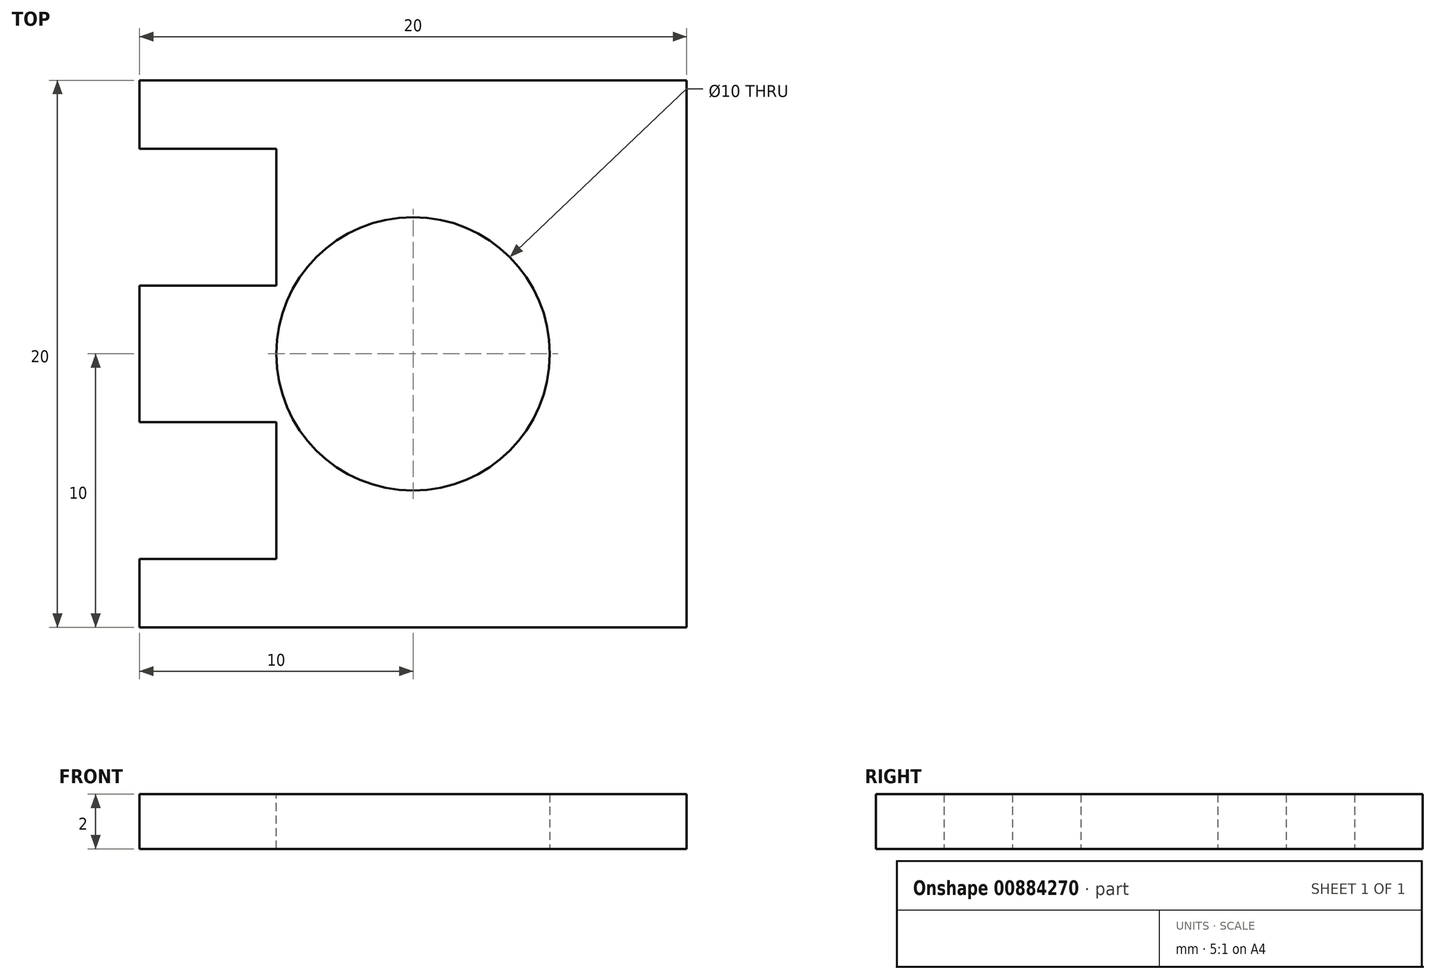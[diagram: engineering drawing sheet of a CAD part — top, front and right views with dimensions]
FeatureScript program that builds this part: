
annotation { "Feature Type Name" : "Feature", "Feature Type Description" : "" }
export const myFeature = defineFeature(function(context is Context, id is Id, definition is map)
    precondition{}
    {
        {
            var Q0;
            Q0=qCreatedBy(makeId("Top.planeOp"),FACE);
            var sketch = newSketch(context, id + "F0", { "sketchPlane" : qUnion([Q0])});
            skLineSegment(sketch, "E0.bottom", {"start": v(10, -10) * mm, "end": v(-10, -10) * mm});
            skLineSegment(sketch, "E0.top", {"start": v(10, 10) * mm, "end": v(-10, 10) * mm});
            skLineSegment(sketch, "E0.left", {"start": v(10, -10) * mm, "end": v(10, 10) * mm});
            skLineSegment(sketch, "E0.right", {"start": v(-10, -10) * mm, "end": v(-10, 10) * mm});
            skPoint(sketch, "E0.middle", {"position": v(0, 0) * mm});
            skCircle(sketch, "E1", {"center": v(0, 0) * mm, "radius": 5 * mm});
            skSolve(sketch);
        }
        {
            var Q0;
            Q0 = qSketchRegion(id + "F0", true);
            extrude(context, id + "F1", {"entities" : qUnion([Q0]), "depth" : 2 * mm, "offsetDistance" : 25 * mm});
        }
        {
            var Q0;
            Q0=makeQuery(id+"F1.opExtrude","CAP_FACE",FACE,{"disambiguationData":[OSD([sQuery(id+"F0.wireOp",EDGE,"E0.bottom"),sQuery(id+"F0.wireOp",EDGE,"E0.top"),sQuery(id+"F0.wireOp",EDGE,"E0.left"),sQuery(id+"F0.wireOp",EDGE,"E0.right"),sQuery(id+"F0.wireOp",EDGE,"E1")])],"isStart":false});
            var sketch = newSketch(context, id + "F2", { "sketchPlane" : qUnion([Q0])});
            skLineSegment(sketch, "E2.0", {"start": v(-10, -10) * mm, "end": v(-10, 10) * mm});
            skLineSegment(sketch, "E3.bottom", {"start": v(-5, 2.5) * mm, "end": v(-15, 2.5) * mm});
            skLineSegment(sketch, "E3.top", {"start": v(-5, 7.5) * mm, "end": v(-15, 7.5) * mm});
            skLineSegment(sketch, "E3.left", {"start": v(-5, 2.5) * mm, "end": v(-5, 7.5) * mm});
            skLineSegment(sketch, "E3.right", {"start": v(-15, 2.5) * mm, "end": v(-15, 7.5) * mm});
            skPoint(sketch, "E3.middle", {"position": v(-10, 5) * mm});
            skLineSegment(sketch, "E4.bottom", {"start": v(-5, -7.5) * mm, "end": v(-15, -7.5) * mm});
            skLineSegment(sketch, "E4.top", {"start": v(-5, -2.5) * mm, "end": v(-15, -2.5) * mm});
            skLineSegment(sketch, "E4.left", {"start": v(-5, -7.5) * mm, "end": v(-5, -2.5) * mm});
            skLineSegment(sketch, "E4.right", {"start": v(-15, -7.5) * mm, "end": v(-15, -2.5) * mm});
            skPoint(sketch, "E4.middle", {"position": v(-10, -5) * mm});
            skSolve(sketch);
        }
        {
            var Q0;
            Q0 = qSketchRegion(id + "F2", true);
            extrude(context, id + "F3", {"entities" : qUnion([Q0]), "operationType" : NewBodyOperationType.REMOVE, "endBound" : BoundingType.THROUGH_ALL, "oppositeDirection" : true, "depth" : 25 * mm, "offsetDistance" : 25 * mm});
        }
    });
